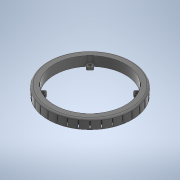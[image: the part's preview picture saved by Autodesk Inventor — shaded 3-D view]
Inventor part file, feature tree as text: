
AUTODESK INVENTOR PART (.ipt)
format: ipt  version: 2020 (Build 240168000, 168)  size: 921,088 bytes
history: native  units: mm
features: extrude x7, projected_geometry x7, sketch x6, pattern_circular x4, fillet x3, other x1
ambient origin geometry x8: Origin, YZ Plane, XZ Plane, XY Plane, X Axis, Y Axis, Z Axis, Center Point
bodies: Body1 (feature_tree)
feature tree (28):
  other  "Твердое тело1"
  sketch  "Эскиз1"
  extrude  "Выдавливание1"  Depth=88.0mm
  extrude  "Выдавливание2"  Depth=5.7mm
  pattern_circular  "Круговой массив1"  [2 undecoded]
  extrude  "Выдавливание3"  Depth=5.5mm
  fillet  "Сопряжение1"  Radius=98.0mm
  extrude  "Выдавливание4"  Depth=84.0mm
  pattern_circular  "Круговой массив2"  [2 undecoded]
  fillet  "Сопряжение2"  Radius=98.0mm
  extrude  "Выдавливание5"  Depth=84.0mm
  pattern_circular  "Круговой массив3"  [2 undecoded]
  extrude  "Выдавливание6"  Depth=10.0mm TaperAngle=0.0deg
  fillet  "Сопряжение3"  Radius=320.0mm
  sketch  "Эскиз6"
  extrude  "Выдавливание7"  Depth=2.0mm
  pattern_circular  "Круговой массив4"  [2 undecoded]
  sketch  "Эскиз2"
  sketch  "Эскиз3"
  projected_geometry  "Спроецированная петля1"
  sketch  "Эскиз4"
  projected_geometry  "Спроецированная петля2"
  sketch  "Эскиз5"
  projected_geometry  "Спроецированная петля3"
  projected_geometry  "Спроецированная петля4"
  projected_geometry  "Спроецированная петля5"
  projected_geometry  "Спроецированная петля6"
  projected_geometry  "Спроецированная петля7"
note: 8 required parameter values undecoded (feature->parameter linkage not recoverable at this tier; creation-order binding heuristic only, values carry confidence <= 0.55)
